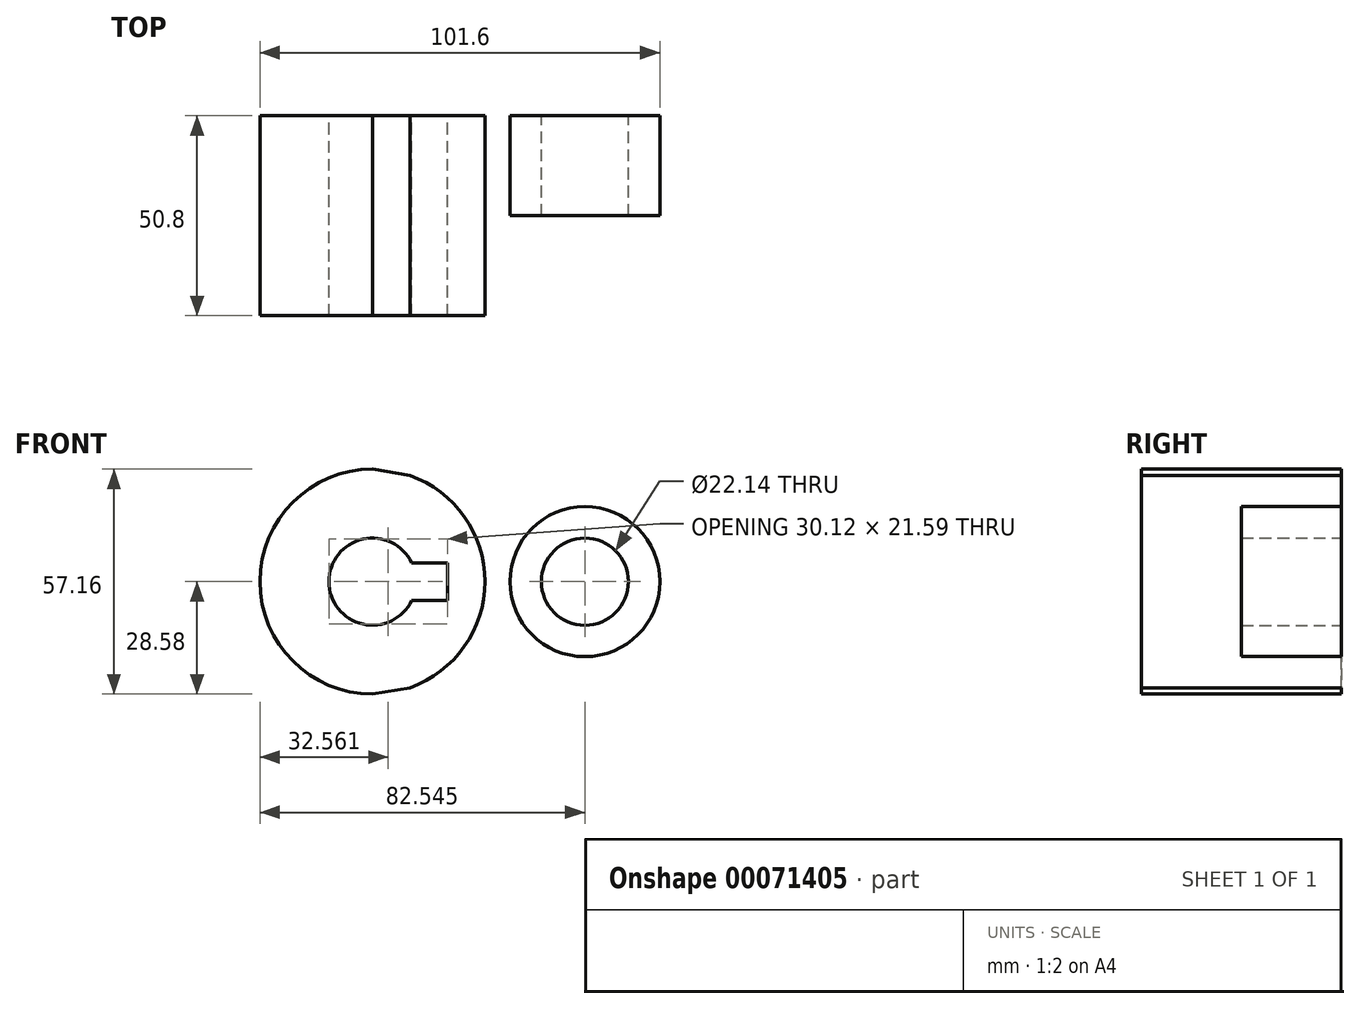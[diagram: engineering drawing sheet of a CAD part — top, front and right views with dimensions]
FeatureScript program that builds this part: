
annotation { "Feature Type Name" : "Feature", "Feature Type Description" : "" }
export const myFeature = defineFeature(function(context is Context, id is Id, definition is map)
    precondition{}
    {
        {
            var Q0;
            Q0=qCreatedBy(makeId("Front.planeOp"),FACE);
            var sketch = newSketch(context, id + "F0", { "sketchPlane" : qUnion([Q0])});
            skCircle(sketch, "E0", {"center": v(0, 0) * mm, "radius": 28.58 * mm});
            skCircle(sketch, "E1", {"center": v(53.97, 0) * mm, "radius": 19.05 * mm});
            skLineSegment(sketch, "E2", {"start": v(0, 28.58) * mm, "end": v(57.2, 18.78) * mm});
            skLineSegment(sketch, "E3", {"start": v(0, -28.57) * mm, "end": v(57.2, -18.78) * mm});
            skCircle(sketch, "E4", {"center": v(0, 0) * mm, "radius": 11.07 * mm});
            skCircle(sketch, "E5", {"center": v(53.97, 0) * mm, "radius": 11.07 * mm});
            skLineSegment(sketch, "E6.rect.bottom", {"start": v(19.05, 4.76) * mm, "end": v(-19.05, 4.76) * mm});
            skLineSegment(sketch, "E6.rect.top", {"start": v(19.05, -4.76) * mm, "end": v(-19.05, -4.76) * mm});
            skLineSegment(sketch, "E6.rect.left", {"start": v(19.05, 4.76) * mm, "end": v(19.05, -4.76) * mm});
            skLineSegment(sketch, "E6.rect.right", {"start": v(-19.05, 4.76) * mm, "end": v(-19.05, -4.76) * mm});
            skSolve(sketch);
        }
        {
            var Q0;
            {var subQ5=sQuery(id+"F0.wireOp",EDGE,"E6.rect.right");Q0=makeQuery(id+"F0.imprint","IMPRINT",FACE,{"disambiguationData":[TD([[makeQuery(id+"F0.imprint","IMPRINT",EDGE,{"derivedFrom":subQ5}),1.0]])]});}
            var Q1;
            {var subQ4=sQuery(id+"F0.wireOp",EDGE,"E6.rect.left");Q1=makeQuery(id+"F0.imprint","IMPRINT",FACE,{"disambiguationData":[TD([[makeQuery(id+"F0.imprint","IMPRINT",EDGE,{"derivedFrom":subQ4}),1.0]])]});}
            var Q2;
            {var subQ0=sQuery(id+"F0.wireOp",EDGE,"E2");var subQ1=sQuery(id+"F0.wireOp",EDGE,"E0");var subQ2=makeQuery(id+"F0.imprint","INTERSECT",VERTEX,{"disambiguationData":[OD(1.0)],"derivedFrom":[subQ1,subQ0]});Q2=makeQuery(id+"F0.imprint","IMPRINT",FACE,{"disambiguationData":[TD([[makeQuery(id+"F0.imprint","IMPRINT",EDGE,{"disambiguationData":[TD([[subQ2,1.0]])],"derivedFrom":subQ1}),-1.0]])]});}
            var Q3;
            Q3=makeQuery(id+"F0.imprint","IMPRINT",FACE,{"disambiguationData":[TD([[makeQuery(id+"F0.imprint","IMPRINT",EDGE,{"derivedFrom":sQuery(id+"F0.wireOp",EDGE,"E5")}),-1.0]])]});
            extrude(context, id + "F1", {"entities" : qUnion([Q0, Q1, Q2, Q3]), "depth" : 25.4 * mm});
        }
        {
            var Q0;
            {var subQ4=sQuery(id+"F0.wireOp",EDGE,"E6.rect.left");Q0=makeQuery(id+"F0.imprint","IMPRINT",FACE,{"disambiguationData":[TD([[makeQuery(id+"F0.imprint","IMPRINT",EDGE,{"derivedFrom":subQ4}),1.0]])]});}
            var Q1;
            {var subQ5=sQuery(id+"F0.wireOp",EDGE,"E6.rect.right");Q1=makeQuery(id+"F0.imprint","IMPRINT",FACE,{"disambiguationData":[TD([[makeQuery(id+"F0.imprint","IMPRINT",EDGE,{"derivedFrom":subQ5}),1.0]])]});}
            extrude(context, id + "F2", {"entities" : qUnion([Q0, Q1]), "operationType" : NewBodyOperationType.ADD, "depth" : 50.8 * mm});
        }
    });
